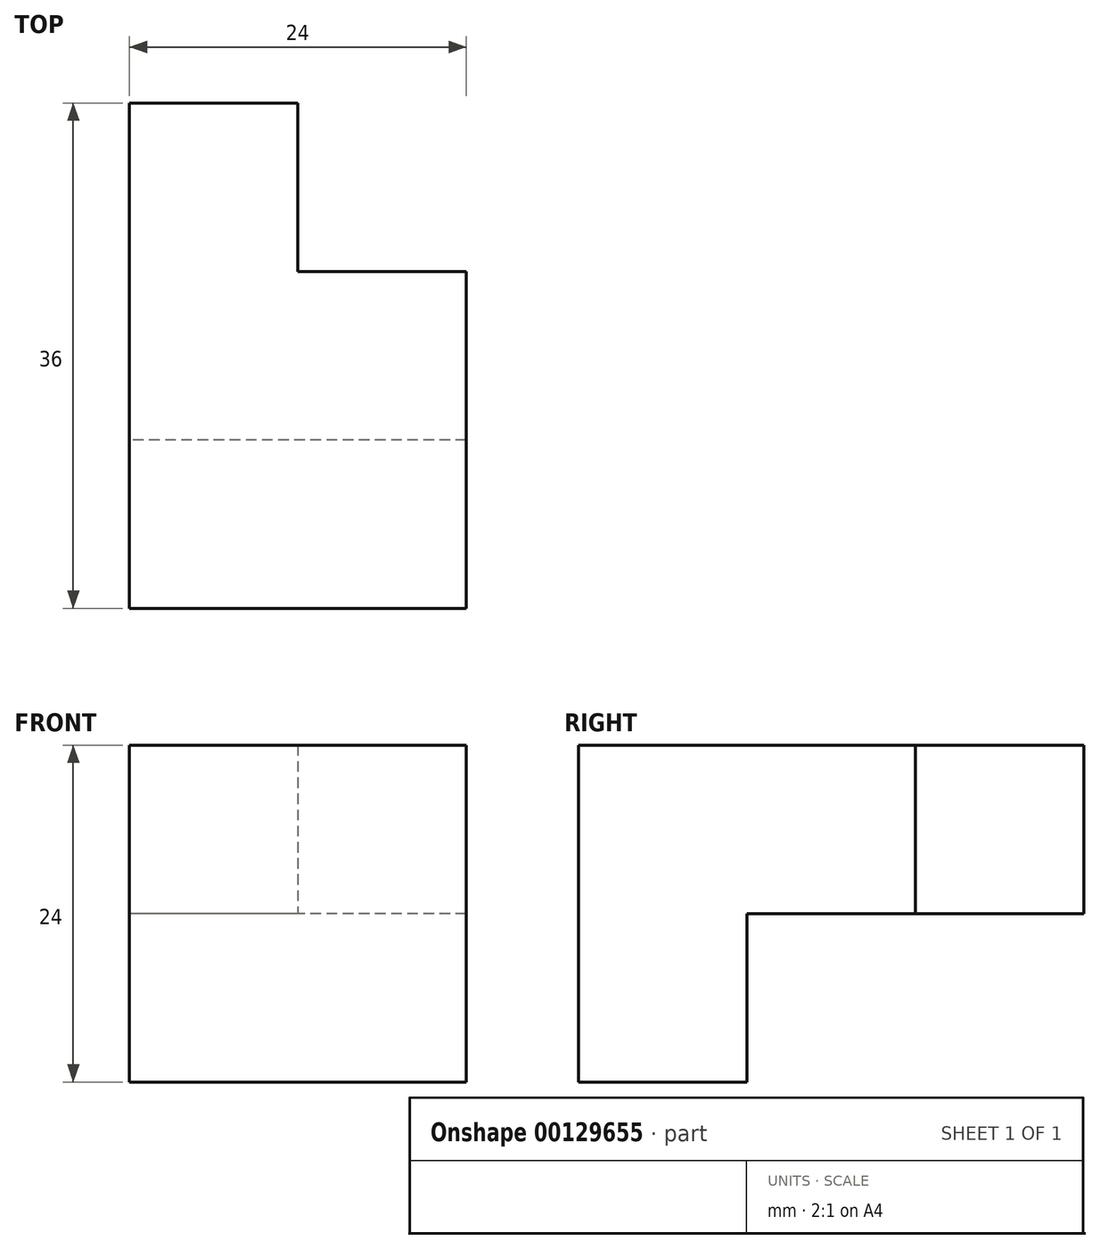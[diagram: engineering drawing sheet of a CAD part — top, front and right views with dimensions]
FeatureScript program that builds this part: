
annotation { "Feature Type Name" : "Feature", "Feature Type Description" : "" }
export const myFeature = defineFeature(function(context is Context, id is Id, definition is map)
    precondition{}
    {
        {
            var Q0;
            Q0=qCreatedBy(makeId("Top.planeOp"),FACE);
            var sketch = newSketch(context, id + "F0", { "sketchPlane" : qUnion([Q0])});
            skLineSegment(sketch, "E0.bottom", {"start": v(-41.58, -34.58) * mm, "end": v(-29.58, -34.58) * mm});
            skLineSegment(sketch, "E0.top", {"start": v(-41.58, -46.58) * mm, "end": v(-29.58, -46.58) * mm});
            skLineSegment(sketch, "E0.left", {"start": v(-41.58, -34.58) * mm, "end": v(-41.58, -46.58) * mm});
            skLineSegment(sketch, "E0.right", {"start": v(-29.58, -34.58) * mm, "end": v(-29.58, -46.58) * mm});
            skLineSegment(sketch, "E1.bottom", {"start": v(-29.58, -46.58) * mm, "end": v(-17.58, -46.58) * mm});
            skLineSegment(sketch, "E1.top", {"start": v(-29.58, -34.58) * mm, "end": v(-17.58, -34.58) * mm});
            skLineSegment(sketch, "E1.left", {"start": v(-29.58, -46.58) * mm, "end": v(-29.58, -34.58) * mm});
            skLineSegment(sketch, "E1.right", {"start": v(-17.58, -46.58) * mm, "end": v(-17.58, -34.58) * mm});
            skSolve(sketch);
        }
        {
            var Q0;
            Q0 = qSketchRegion(id + "F0", true);
            extrude(context, id + "F1", {"entities" : qUnion([Q0]), "depth" : 12 * mm});
        }
        {
            var Q0;
            Q0=makeQuery(id+"F1.opExtrude","CAP_FACE",FACE,{"disambiguationData":[OSD([sQuery(id+"F0.wireOp",EDGE,"E0.bottom"),sQuery(id+"F0.wireOp",EDGE,"E0.top"),sQuery(id+"F0.wireOp",EDGE,"E0.left"),sQuery(id+"F0.wireOp",EDGE,"E1.bottom"),sQuery(id+"F0.wireOp",EDGE,"E1.top"),sQuery(id+"F0.wireOp",EDGE,"E1.right")])],"isStart":false});
            var sketch = newSketch(context, id + "F2", { "sketchPlane" : qUnion([Q0])});
            skLineSegment(sketch, "E2.bottom", {"start": v(-41.58, -34.58) * mm, "end": v(-17.58, -34.58) * mm});
            skLineSegment(sketch, "E2.top", {"start": v(-41.58, -46.58) * mm, "end": v(-17.58, -46.58) * mm});
            skLineSegment(sketch, "E2.left", {"start": v(-41.58, -34.58) * mm, "end": v(-41.58, -46.58) * mm});
            skLineSegment(sketch, "E2.right", {"start": v(-17.58, -34.58) * mm, "end": v(-17.58, -46.58) * mm});
            skSolve(sketch);
        }
        {
            var Q0;
            Q0 = qSketchRegion(id + "F2", true);
            extrude(context, id + "F3", {"entities" : qUnion([Q0]), "operationType" : NewBodyOperationType.ADD, "depth" : 12 * mm});
        }
        {
            var Q0;
            Q0=makeQuery(id+"F3.boolean.opBoolean","MERGE",FACE,{"derivedFrom":[makeQuery(id+"F1.opExtrude","SWEPT_FACE",FACE,{"disambiguationData":[OSD([sQuery(id+"F0.wireOp",EDGE,"E0.bottom"),sQuery(id+"F0.wireOp",EDGE,"E1.top")])]}),makeQuery(id+"F3.opExtrude","SWEPT_FACE",FACE,{"disambiguationData":[OSD([sQuery(id+"F2.wireOp",EDGE,"E2.bottom")])]})]});
            var sketch = newSketch(context, id + "F4", { "sketchPlane" : qUnion([Q0])});
            skLineSegment(sketch, "E3.bottom", {"start": v(17.58, 24) * mm, "end": v(41.58, 24) * mm});
            skLineSegment(sketch, "E3.top", {"start": v(17.58, 12) * mm, "end": v(41.58, 12) * mm});
            skLineSegment(sketch, "E3.left", {"start": v(17.58, 24) * mm, "end": v(17.58, 12) * mm});
            skLineSegment(sketch, "E3.right", {"start": v(41.58, 24) * mm, "end": v(41.58, 12) * mm});
            skSolve(sketch);
        }
        {
            var Q0;
            Q0 = qSketchRegion(id + "F4", true);
            extrude(context, id + "F5", {"entities" : qUnion([Q0]), "operationType" : NewBodyOperationType.ADD, "depth" : 12 * mm});
        }
        {
            var Q0;
            Q0=makeQuery(id+"F5.opExtrude","CAP_FACE",FACE,{"disambiguationData":[OSD([sQuery(id+"F4.wireOp",EDGE,"E3.bottom"),sQuery(id+"F4.wireOp",EDGE,"E3.top"),sQuery(id+"F4.wireOp",EDGE,"E3.left"),sQuery(id+"F4.wireOp",EDGE,"E3.right")])],"isStart":false});
            var sketch = newSketch(context, id + "F6", { "sketchPlane" : qUnion([Q0])});
            skLineSegment(sketch, "E4.bottom", {"start": v(29.58, 24) * mm, "end": v(41.58, 24) * mm});
            skLineSegment(sketch, "E4.top", {"start": v(29.58, 12) * mm, "end": v(41.58, 12) * mm});
            skLineSegment(sketch, "E4.left", {"start": v(29.58, 24) * mm, "end": v(29.58, 12) * mm});
            skLineSegment(sketch, "E4.right", {"start": v(41.58, 24) * mm, "end": v(41.58, 12) * mm});
            skSolve(sketch);
        }
        {
            var Q0;
            Q0 = qSketchRegion(id + "F6", true);
            extrude(context, id + "F7", {"entities" : qUnion([Q0]), "operationType" : NewBodyOperationType.ADD, "depth" : 12 * mm});
        }
    });
